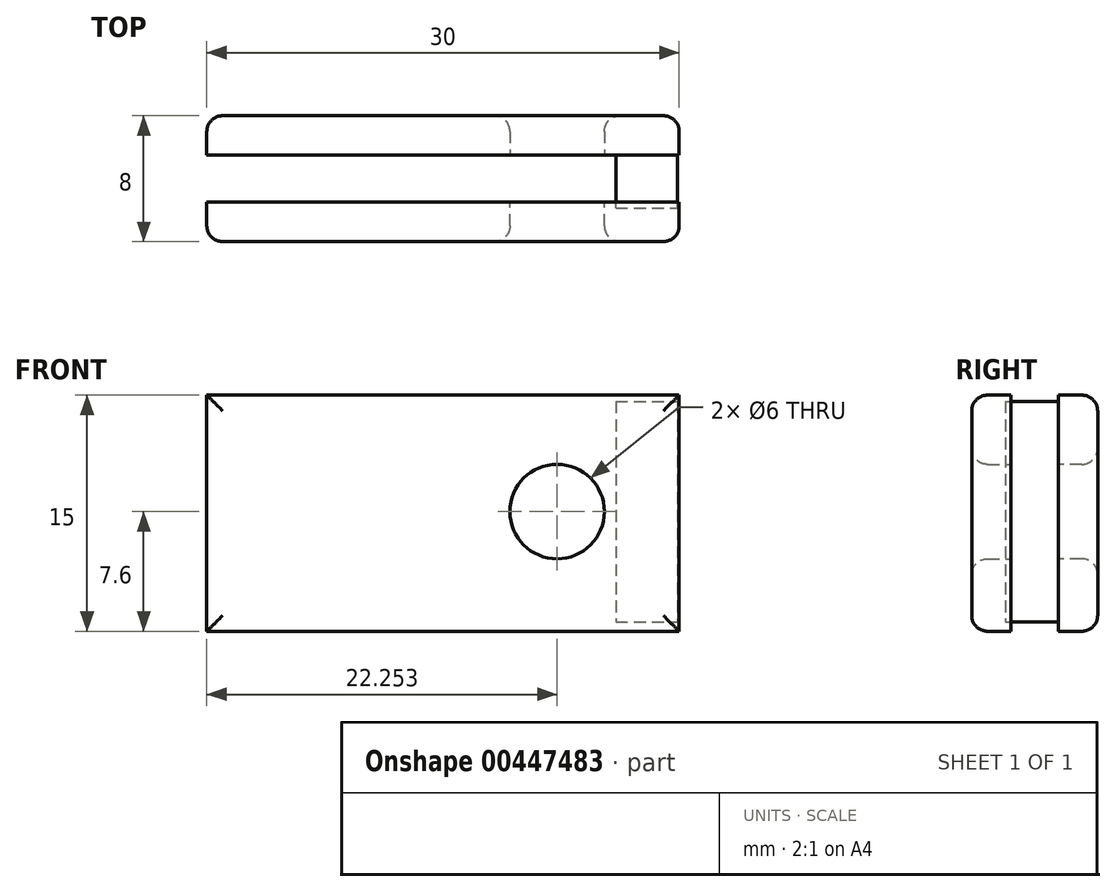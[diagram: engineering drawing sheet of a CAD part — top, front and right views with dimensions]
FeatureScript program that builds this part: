
annotation { "Feature Type Name" : "Feature", "Feature Type Description" : "" }
export const myFeature = defineFeature(function(context is Context, id is Id, definition is map)
    precondition{}
    {
        {
            var Q0;
            Q0=qCreatedBy(makeId("Front.planeOp"),FACE);
            var sketch = newSketch(context, id + "F0", { "sketchPlane" : qUnion([Q0])});
            skLineSegment(sketch, "E0.bottom", {"start": v(-16.48, 7.4) * mm, "end": v(13.52, 7.4) * mm});
            skLineSegment(sketch, "E0.top", {"start": v(-16.48, -7.6) * mm, "end": v(13.52, -7.6) * mm});
            skLineSegment(sketch, "E0.left", {"start": v(-16.48, 7.4) * mm, "end": v(-16.48, -7.6) * mm});
            skLineSegment(sketch, "E0.right", {"start": v(13.52, 7.4) * mm, "end": v(13.52, -7.6) * mm});
            skSolve(sketch);
        }
        {
            var Q0;
            Q0 = qSketchRegion(id + "F0", true);
            extrude(context, id + "F1", {"entities" : qUnion([Q0]), "depth" : 2.5 * mm, "offsetDistance" : 25 * mm});
        }
        {
            var Q0;
            Q0=qCreatedBy(makeId("Front.planeOp"),FACE);
            var sketch = newSketch(context, id + "F2", { "sketchPlane" : qUnion([Q0])});
            skCircle(sketch, "E1", {"center": v(5.77, 0) * mm, "radius": 3 * mm});
            skSolve(sketch);
        }
        {
            var Q0;
            Q0 = qSketchRegion(id + "F2", true);
            extrude(context, id + "F3", {"entities" : qUnion([Q0]), "operationType" : NewBodyOperationType.REMOVE, "depth" : 25 * mm, "offsetDistance" : 25 * mm});
        }
        {
            var Q0;
            Q0=makeQuery(id+"F1.opExtrude","CAP_FACE",FACE,{"disambiguationData":[OSD([sQuery(id+"F0.wireOp",EDGE,"E0.bottom"),sQuery(id+"F0.wireOp",EDGE,"E0.top"),sQuery(id+"F0.wireOp",EDGE,"E0.left"),sQuery(id+"F0.wireOp",EDGE,"E0.right")])],"isStart":false});
            fillet(context, id + "F4", {"entities" : qUnion([Q0]), "tangentPropagation" : true, "radius" : 1 * mm, "defaultsChanged" : true, "vertexSettings" : [], "allowEdgeOverflow" : false});
        }
        {
            var Q0;
            Q0=makeQuery(id+"F1.opExtrude","SWEPT_BODY",BODY,{"disambiguationData":[OSD([sQuery(id+"F0.wireOp",EDGE,"E0.bottom"),sQuery(id+"F0.wireOp",EDGE,"E0.top"),sQuery(id+"F0.wireOp",EDGE,"E0.left"),sQuery(id+"F0.wireOp",EDGE,"E0.right")])]});
            var Q1;
            Q1=qCreatedBy(makeId("Front.planeOp"),FACE);
            mirror(context, id + "F5", {"entities" : qUnion([Q0]), "mirrorPlane" : qUnion([Q1])});
        }
        {
            var Q0;
            Q0=makeQuery(id+"F1.opExtrude","SWEPT_BODY",BODY,{"disambiguationData":[OSD([sQuery(id+"F0.wireOp",EDGE,"E0.bottom"),sQuery(id+"F0.wireOp",EDGE,"E0.top"),sQuery(id+"F0.wireOp",EDGE,"E0.left"),sQuery(id+"F0.wireOp",EDGE,"E0.right")])]});
            transform(context, id + "F6", {"entities" : qUnion([Q0]), "transformType" : TransformType.TRANSLATION_3D, "dx" : 0 * mm, "dy" : -3 * mm, "dz" : 0 * mm, "makeCopy" : false});
        }
        {
            var Q0;
            Q0=qCreatedBy(makeId("Top.planeOp"),FACE);
            var sketch = newSketch(context, id + "F7", { "sketchPlane" : qUnion([Q0])});
            skLineSegment(sketch, "E2.bottom", {"start": v(9.5, -3.36) * mm, "end": v(13.42, -3.36) * mm});
            skLineSegment(sketch, "E2.top", {"start": v(9.5, 0) * mm, "end": v(13.42, 0) * mm});
            skLineSegment(sketch, "E2.left", {"start": v(9.5, -3.36) * mm, "end": v(9.5, 0) * mm});
            skLineSegment(sketch, "E2.right", {"start": v(13.42, -3.36) * mm, "end": v(13.42, 0) * mm});
            skSolve(sketch);
        }
        {
            var Q0;
            Q0 = qSketchRegion(id + "F7", true);
            extrude(context, id + "F8", {"entities" : qUnion([Q0]), "depth" : 14 * mm, "offsetDistance" : 25 * mm, "symmetric" : true});
        }
        {
            var Q0;
            Q0=qCreatedBy(makeId("Front.planeOp"), FACE);
            var sketch = newSketch(context, id + "F9", { "sketchPlane" : qUnion([Q0])});
            skLineSegment(sketch, "E3", {"start": v(-67.59, -43.51) * mm, "end": v(17.9, 38.85) * mm});
            skPoint(sketch, "E4", {"position": v(24.63, 36.17) * mm});
            skSolve(sketch);
        }
    });
